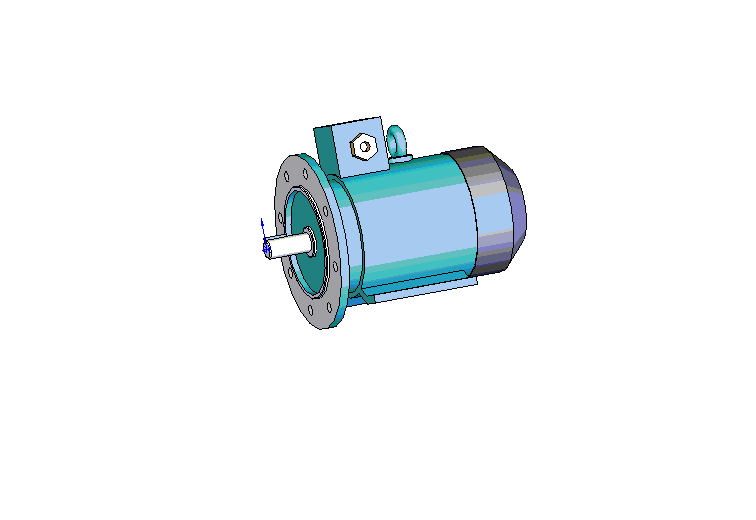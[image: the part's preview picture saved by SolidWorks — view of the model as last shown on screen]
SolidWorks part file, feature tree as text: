
SOLIDWORKS PART (.sldprt)
format: sldprt  version: not decoded by parser v0  size: 694,784 bytes
history: native  units: mm
features: sketch x18, extrude x12, plane x4, chamfer x4, cut_extrude x4, material x1, sweep x1 (+10 scaffold rows collapsed)
feature tree (54):
  scaffold x10  (default folders/planes/origin — collapsed)
  material  "Ст.3 ГОСТ 380-88"
  plane  "Спереди"
  plane  "Сверху"
  plane  "Справа"
  sketch  "Эскиз1"  dims[D1=22.0mm]
  extrude  "Вытянуть1"  Depth=50mm
  sketch  "Эскиз2"  dims[D1=6.0mm D2=6.0mm D3=24.5mm]
  extrude  "Вытянуть2"  Depth=25mm
  chamfer  "Фаска1"  Distance=1mm Angle=45deg
  sketch  "Эскиз3"  dims[D1=200.0mm]
  extrude  "Вытянуть3"  Depth=10mm
  sketch  "Эскиз4"  dims[D1=130.0mm D2=120.0mm]
  extrude  "Вытянуть4"  Depth=3.5mm
  sketch  "Эскиз5"  dims[D1=120.0mm D2=36.0mm]
  cut_extrude  "Вырез-Вытянуть1"  Depth=3.5mm
  chamfer  "Фаска2"  Distance=1mm Angle=45deg
  sketch  "Эскиз6"  dims[D1=130.0mm]
  extrude  "Вытянуть5"  Depth=30mm
  sketch  "Эскиз7"  dims[D1=142.0mm]
  extrude  "Вытянуть6"  Depth=137mm
  sketch  "Эскиз8"  dims[D1=~144.496182mm]
  extrude  "Вытянуть7"  Depth=69.5mm
  chamfer  "Фаска3"  Distance=26mm Angle=45deg
  sketch  "Эскиз9"  dims[c1.D2=12.0mm c1.D4=12.0mm c1.D1=~128.009757mm c2.D1=22.5deg c2.D3=82.5mm c2.D4=82.5mm c2.D5=82.5mm]
  cut_extrude  "Вырез-Вытянуть2"  [1 undecoded]
  sketch  "Эскиз10"  dims[c1.D1=9.0mm c1.D2=74.5mm c1.D3=24.0mm c1.D4=9.0mm c1.D5=~41.087468mm c2.D5=60.0deg c2.D6=80.0mm]
  extrude  "Вытянуть8"  Depth=124mm
  sketch  "Эскиз11"  dims[D2=10.0mm D1=100.0mm D3=62.5mm D4=90.0deg D5=200.0mm D6=100.0mm D7=125.0mm]
  cut_extrude  "Вырез-Вытянуть3"  [1 undecoded]
  sketch  "Эскиз12"  dims[D1=60.0mm D2=1.0mm D3=60.0mm]
  extrude  "Вытянуть9"  Depth=124.5mm
  sketch  "Эскиз13"  dims[D1=30.0mm D2=175.0mm]
  extrude  "Вытянуть10"  Depth=76.5mm
  chamfer  "Фаска4"  Distance=1mm Angle=45deg
  plane  "Плоскость1"  Offset=175mm
  sketch  "Эскиз14"  dims[D1=30.0mm]
  sketch  "Эскиз15"  dims[D1=12.0mm D2=15.0mm]
  sweep  "По траектории1"
  sketch  "Эскиз16"  dims[D1=16.0mm D2=30.0mm D3=30.0mm]
  extrude  "Вытянуть11"  Depth=6mm
  sketch  "Эскиз17"  dims[D1=30.0mm]
  extrude  "Вытянуть12"  Depth=10mm
  sketch  "Эскиз18"  dims[D1=12.0mm]
  cut_extrude  "Вырез-Вытянуть4"  Depth=10mm
decode coverage: 36 of 39 modeling features carry decoded parameters
note: ~ marks probable driven/reference dimensions
note: 2 parameter values undecoded
note: suppression state not decoded; provenance and decode notes live in map.json
